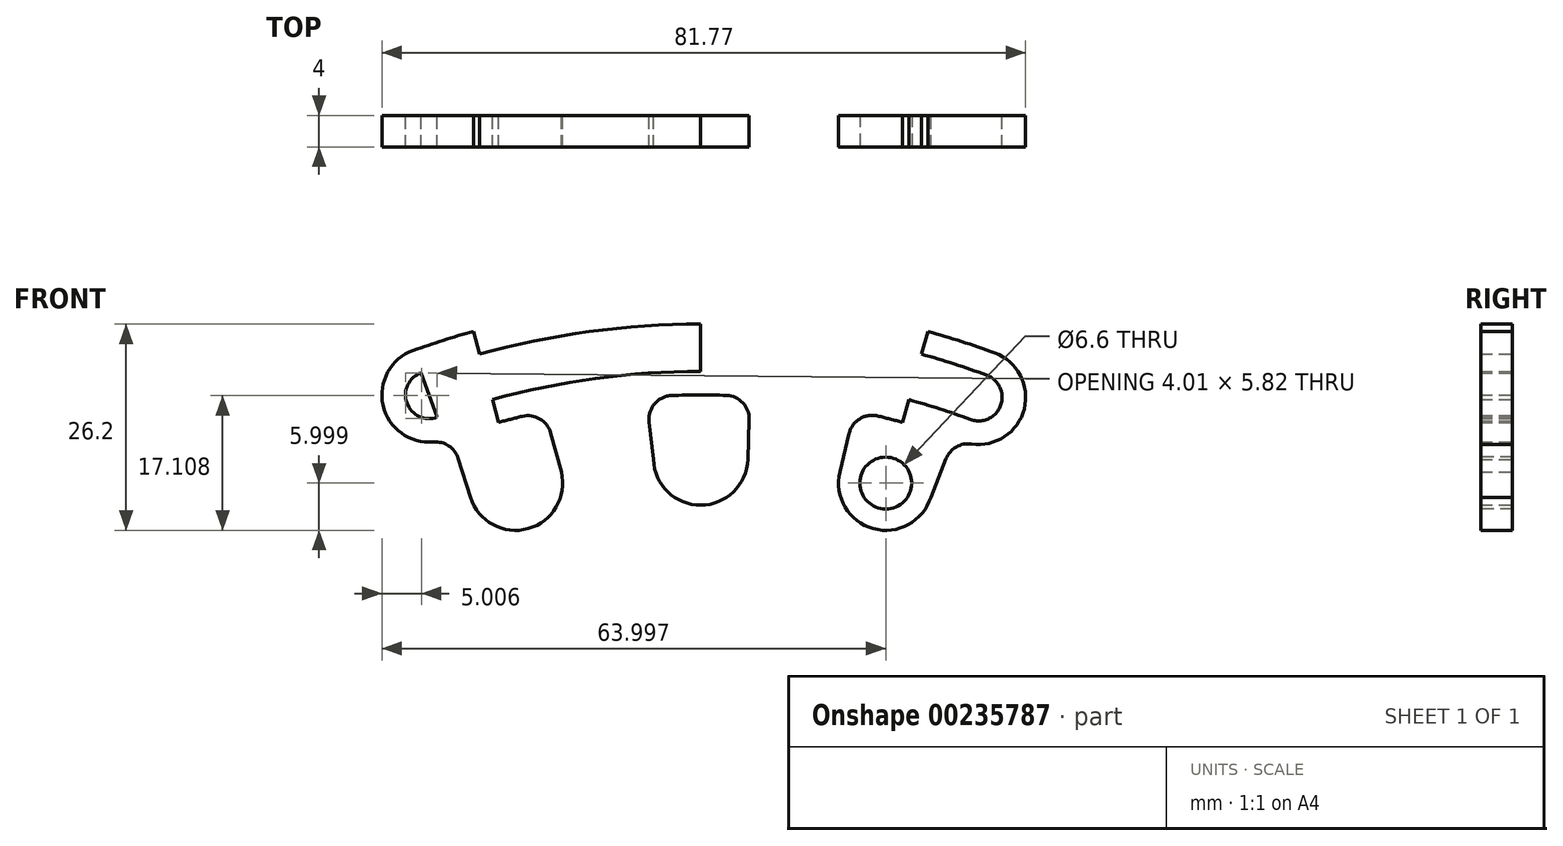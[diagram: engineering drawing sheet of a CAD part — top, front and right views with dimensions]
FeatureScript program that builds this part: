
annotation { "Feature Type Name" : "Feature", "Feature Type Description" : "" }
export const myFeature = defineFeature(function(context is Context, id is Id, definition is map)
    precondition{}
    {
        {
            var Q0;
            Q0=qCreatedBy(makeId("Front.planeOp"),FACE);
            var sketch = newSketch(context, id + "F0", { "sketchPlane" : qUnion([Q0])});
            skArc(sketch, "E0", {"start": v(-36.51, 101.64) * mm, "mid": v(0.45, 108) * mm, "end": v(37.36, 101.33) * mm});
            skLineSegment(sketch, "E1", {"start": v(-36.51, 101.64) * mm, "end": v(0, 0) * mm});
            skLineSegment(sketch, "E2", {"start": v(37.36, 101.33) * mm, "end": v(0, 0) * mm});
            skArc(sketch, "E3", {"start": v(-35.5, 98.82) * mm, "mid": v(0.44, 105) * mm, "end": v(36.33, 98.52) * mm});
            skArc(sketch, "E4", {"start": v(-33.47, 93.17) * mm, "mid": v(0.42, 99) * mm, "end": v(34.25, 92.89) * mm});
            skArc(sketch, "E5", {"start": v(-35.5, 98.82) * mm, "mid": v(-37.3, 94.98) * mm, "end": v(-33.47, 93.17) * mm});
            skArc(sketch, "E6", {"start": v(34.25, 92.89) * mm, "mid": v(38.1, 94.66) * mm, "end": v(36.33, 98.52) * mm});
            skLineSegment(sketch, "E7", {"start": v(0, 0) * mm, "end": v(28.86, 104.07) * mm});
            skLineSegment(sketch, "E8", {"start": v(0, 0) * mm, "end": v(-28.86, 104.07) * mm});
            skLineSegment(sketch, "E9", {"start": v(0, 0) * mm, "end": v(0, 108) * mm});
            skArc(sketch, "E10", {"start": v(-29.75, 82.82) * mm, "mid": v(0.37, 88) * mm, "end": v(30.44, 82.57) * mm});
            skArc(sketch, "E11", {"start": v(-6, 87.8) * mm, "mid": v(0, 82) * mm, "end": v(6, 87.8) * mm});
            skArc(sketch, "E12", {"start": v(-36.51, 101.64) * mm, "mid": v(-40.13, 93.97) * mm, "end": v(-32.45, 90.35) * mm});
            skArc(sketch, "E13", {"start": v(37.36, 101.33) * mm, "mid": v(40.92, 93.63) * mm, "end": v(33.21, 90.07) * mm});
            skArc(sketch, "E14.0", {"start": v(-32.45, 90.35) * mm, "mid": v(0.4, 96) * mm, "end": v(33.21, 90.07) * mm});
            skArc(sketch, "E15", {"start": v(-29.24, 83) * mm, "mid": v(-21.91, 79.02) * mm, "end": v(-17.68, 86.2) * mm});
            skArc(sketch, "E16", {"start": v(17.68, 86.2) * mm, "mid": v(21.91, 79.02) * mm, "end": v(29.24, 83) * mm});
            skLineSegment(sketch, "E17", {"start": v(17.68, 86.2) * mm, "end": v(19.56, 93.99) * mm});
            skLineSegment(sketch, "E18", {"start": v(29.24, 83) * mm, "end": v(32.2, 90.44) * mm});
            skLineSegment(sketch, "E19", {"start": v(-6, 87.8) * mm, "end": v(-6.9, 95.75) * mm});
            skLineSegment(sketch, "E20", {"start": v(-17.68, 86.2) * mm, "end": v(-19.83, 93.93) * mm});
            skLineSegment(sketch, "E21", {"start": v(-29.24, 83) * mm, "end": v(-31.64, 90.64) * mm});
            skLineSegment(sketch, "E22", {"start": v(6, 87.8) * mm, "end": v(6.27, 95.8) * mm});
            skSolve(sketch);
        }
        {
            var Q0;
            {var subQ4=sQuery(id+"F0.wireOp",EDGE,"E4");var subQ6=sQuery(id+"F0.wireOp",EDGE,"E8");var subQ7=makeQuery(id+"F0.imprint","INTERSECT",VERTEX,{"derivedFrom":[subQ4,subQ6]});Q0=makeQuery(id+"F0.imprint","IMPRINT",FACE,{"disambiguationData":[TD([[makeQuery(id+"F0.imprint","IMPRINT",EDGE,{"disambiguationData":[TD([[subQ7,1.0]])],"derivedFrom":subQ6}),1.0]])]});}
            var Q1;
            {var subQ2=sQuery(id+"F0.wireOp",EDGE,"E8");var subQ5=sQuery(id+"F0.wireOp",EDGE,"E4");var subQ8=makeQuery(id+"F0.imprint","INTERSECT",VERTEX,{"derivedFrom":[subQ5,subQ2]});Q1=makeQuery(id+"F0.imprint","IMPRINT",FACE,{"disambiguationData":[TD([[makeQuery(id+"F0.imprint","IMPRINT",EDGE,{"disambiguationData":[TD([[subQ8,-1.0]])],"derivedFrom":subQ5}),-1.0]])]});}
            var Q2;
            {var subQ5=sQuery(id+"F0.wireOp",EDGE,"E20");Q2=makeQuery(id+"F0.imprint","IMPRINT",FACE,{"disambiguationData":[TD([[makeQuery(id+"F0.imprint","IMPRINT",EDGE,{"derivedFrom":subQ5}),1.0]])]});}
            var Q3;
            {var subQ5=sQuery(id+"F0.wireOp",EDGE,"E21");Q3=makeQuery(id+"F0.imprint","IMPRINT",FACE,{"disambiguationData":[TD([[makeQuery(id+"F0.imprint","IMPRINT",EDGE,{"derivedFrom":subQ5}),-1.0]])]});}
            var Q4;
            {var subQ0=sQuery(id+"F0.wireOp",EDGE,"E15");var subQ1=sQuery(id+"F0.wireOp",EDGE,"E8");var subQ2=makeQuery(id+"F0.imprint","INTERSECT",VERTEX,{"derivedFrom":[subQ1,subQ0]});Q4=makeQuery(id+"F0.imprint","IMPRINT",FACE,{"disambiguationData":[TD([[makeQuery(id+"F0.imprint","IMPRINT",EDGE,{"disambiguationData":[TD([[subQ2,-1.0]])],"derivedFrom":subQ1}),1.0]])]});}
            var Q5;
            {var subQ0=sQuery(id+"F0.wireOp",EDGE,"E15");var subQ1=sQuery(id+"F0.wireOp",EDGE,"E8");var subQ2=makeQuery(id+"F0.imprint","INTERSECT",VERTEX,{"derivedFrom":[subQ1,subQ0]});Q5=makeQuery(id+"F0.imprint","IMPRINT",FACE,{"disambiguationData":[TD([[makeQuery(id+"F0.imprint","IMPRINT",EDGE,{"disambiguationData":[TD([[subQ2,-1.0]])],"derivedFrom":subQ1}),-1.0]])]});}
            var Q6;
            {var subQ5=sQuery(id+"F0.wireOp",EDGE,"E19");Q6=makeQuery(id+"F0.imprint","IMPRINT",FACE,{"disambiguationData":[TD([[makeQuery(id+"F0.imprint","IMPRINT",EDGE,{"derivedFrom":subQ5}),-1.0]])]});}
            var Q7;
            {var subQ5=sQuery(id+"F0.wireOp",EDGE,"E22");Q7=makeQuery(id+"F0.imprint","IMPRINT",FACE,{"disambiguationData":[TD([[makeQuery(id+"F0.imprint","IMPRINT",EDGE,{"derivedFrom":subQ5}),1.0]])]});}
            var Q8;
            {var subQ0=sQuery(id+"F0.wireOp",EDGE,"E11");var subQ1=sQuery(id+"F0.wireOp",EDGE,"E9");var subQ2=makeQuery(id+"F0.imprint","INTERSECT",VERTEX,{"derivedFrom":[subQ1,subQ0]});Q8=makeQuery(id+"F0.imprint","IMPRINT",FACE,{"disambiguationData":[TD([[makeQuery(id+"F0.imprint","IMPRINT",EDGE,{"disambiguationData":[TD([[subQ2,-1.0]])],"derivedFrom":subQ1}),-1.0]])]});}
            var Q9;
            {var subQ0=sQuery(id+"F0.wireOp",EDGE,"E11");var subQ1=sQuery(id+"F0.wireOp",EDGE,"E9");var subQ2=makeQuery(id+"F0.imprint","INTERSECT",VERTEX,{"derivedFrom":[subQ1,subQ0]});Q9=makeQuery(id+"F0.imprint","IMPRINT",FACE,{"disambiguationData":[TD([[makeQuery(id+"F0.imprint","IMPRINT",EDGE,{"disambiguationData":[TD([[subQ2,-1.0]])],"derivedFrom":subQ1}),1.0]])]});}
            var Q10;
            {var subQ2=sQuery(id+"F0.wireOp",EDGE,"E9");var subQ4=sQuery(id+"F0.wireOp",EDGE,"E4");var subQ5=makeQuery(id+"F0.imprint","INTERSECT",VERTEX,{"derivedFrom":[subQ4,subQ2]});Q10=makeQuery(id+"F0.imprint","IMPRINT",FACE,{"disambiguationData":[TD([[makeQuery(id+"F0.imprint","IMPRINT",EDGE,{"disambiguationData":[TD([[subQ5,-1.0]])],"derivedFrom":subQ4}),-1.0]])]});}
            var Q11;
            {var subQ2=sQuery(id+"F0.wireOp",EDGE,"E5");Q11=makeQuery(id+"F0.imprint","IMPRINT",FACE,{"disambiguationData":[TD([[makeQuery(id+"F0.imprint","IMPRINT",EDGE,{"derivedFrom":subQ2}),-1.0]])]});}
            var Q12;
            {var subQ1=sQuery(id+"F0.wireOp",EDGE,"E0");var subQ3=sQuery(id+"F0.wireOp",EDGE,"E8");var subQ4=makeQuery(id+"F0.imprint","INTERSECT",VERTEX,{"derivedFrom":[subQ1,subQ3]});Q12=makeQuery(id+"F0.imprint","IMPRINT",FACE,{"disambiguationData":[TD([[makeQuery(id+"F0.imprint","IMPRINT",EDGE,{"disambiguationData":[TD([[subQ4,1.0]])],"derivedFrom":subQ3}),1.0]])]});}
            var Q13;
            {var subQ0=sQuery(id+"F0.wireOp",EDGE,"E8");var subQ1=sQuery(id+"F0.wireOp",EDGE,"E0");var subQ2=makeQuery(id+"F0.imprint","INTERSECT",VERTEX,{"derivedFrom":[subQ1,subQ0]});Q13=makeQuery(id+"F0.imprint","IMPRINT",FACE,{"disambiguationData":[TD([[makeQuery(id+"F0.imprint","IMPRINT",EDGE,{"disambiguationData":[TD([[subQ2,-1.0]])],"derivedFrom":subQ1}),-1.0]])]});}
            var Q14;
            {var subQ0=sQuery(id+"F0.wireOp",EDGE,"E7");var subQ1=sQuery(id+"F0.wireOp",EDGE,"E0");var subQ2=makeQuery(id+"F0.imprint","INTERSECT",VERTEX,{"derivedFrom":[subQ1,subQ0]});Q14=makeQuery(id+"F0.imprint","IMPRINT",FACE,{"disambiguationData":[TD([[makeQuery(id+"F0.imprint","IMPRINT",EDGE,{"disambiguationData":[TD([[subQ2,1.0]])],"derivedFrom":subQ1}),-1.0]])]});}
            var Q15;
            {var subQ1=sQuery(id+"F0.wireOp",EDGE,"E0");var subQ3=sQuery(id+"F0.wireOp",EDGE,"E7");var subQ4=makeQuery(id+"F0.imprint","INTERSECT",VERTEX,{"derivedFrom":[subQ1,subQ3]});Q15=makeQuery(id+"F0.imprint","IMPRINT",FACE,{"disambiguationData":[TD([[makeQuery(id+"F0.imprint","IMPRINT",EDGE,{"disambiguationData":[TD([[subQ4,1.0]])],"derivedFrom":subQ3}),-1.0]])]});}
            var Q16;
            {var subQ2=sQuery(id+"F0.wireOp",EDGE,"E6");Q16=makeQuery(id+"F0.imprint","IMPRINT",FACE,{"disambiguationData":[TD([[makeQuery(id+"F0.imprint","IMPRINT",EDGE,{"derivedFrom":subQ2}),-1.0]])]});}
            var Q17;
            {var subQ0=sQuery(id+"F0.wireOp",EDGE,"E7");var subQ1=sQuery(id+"F0.wireOp",EDGE,"E4");var subQ2=makeQuery(id+"F0.imprint","INTERSECT",VERTEX,{"derivedFrom":[subQ1,subQ0]});Q17=makeQuery(id+"F0.imprint","IMPRINT",FACE,{"disambiguationData":[TD([[makeQuery(id+"F0.imprint","IMPRINT",EDGE,{"disambiguationData":[TD([[subQ2,1.0]])],"derivedFrom":subQ0}),-1.0]])]});}
            var Q18;
            {var subQ5=sQuery(id+"F0.wireOp",EDGE,"E18");Q18=makeQuery(id+"F0.imprint","IMPRINT",FACE,{"disambiguationData":[TD([[makeQuery(id+"F0.imprint","IMPRINT",EDGE,{"derivedFrom":subQ5}),1.0]])]});}
            var Q19;
            {var subQ5=sQuery(id+"F0.wireOp",EDGE,"E17");Q19=makeQuery(id+"F0.imprint","IMPRINT",FACE,{"disambiguationData":[TD([[makeQuery(id+"F0.imprint","IMPRINT",EDGE,{"derivedFrom":subQ5}),-1.0]])]});}
            var Q20;
            {var subQ0=sQuery(id+"F0.wireOp",EDGE,"E16");var subQ1=sQuery(id+"F0.wireOp",EDGE,"E7");var subQ2=makeQuery(id+"F0.imprint","INTERSECT",VERTEX,{"derivedFrom":[subQ1,subQ0]});Q20=makeQuery(id+"F0.imprint","IMPRINT",FACE,{"disambiguationData":[TD([[makeQuery(id+"F0.imprint","IMPRINT",EDGE,{"disambiguationData":[TD([[subQ2,-1.0]])],"derivedFrom":subQ1}),1.0]])]});}
            var Q21;
            {var subQ0=sQuery(id+"F0.wireOp",EDGE,"E16");var subQ1=sQuery(id+"F0.wireOp",EDGE,"E7");var subQ2=makeQuery(id+"F0.imprint","INTERSECT",VERTEX,{"derivedFrom":[subQ1,subQ0]});Q21=makeQuery(id+"F0.imprint","IMPRINT",FACE,{"disambiguationData":[TD([[makeQuery(id+"F0.imprint","IMPRINT",EDGE,{"disambiguationData":[TD([[subQ2,-1.0]])],"derivedFrom":subQ1}),-1.0]])]});}
            extrude(context, id + "F1", {"entities" : qUnion([Q0, Q1, Q2, Q3, Q4, Q5, Q6, Q7, Q8, Q9, Q10, Q11, Q12, Q13, Q14, Q15, Q16, Q17, Q18, Q19, Q20, Q21]), "depth" : 4 * mm});
        }
        {
            var Q0;
            Q0=makeQuery(id+"F1.opExtrude","CAP_FACE",FACE,{"disambiguationData":[OSD([sQuery(id+"F0.wireOp",EDGE,"E0"),sQuery(id+"F0.wireOp",EDGE,"E3"),sQuery(id+"F0.wireOp",EDGE,"E4"),sQuery(id+"F0.wireOp",EDGE,"E5"),sQuery(id+"F0.wireOp",EDGE,"E6"),sQuery(id+"F0.wireOp",EDGE,"E11"),sQuery(id+"F0.wireOp",EDGE,"E12"),sQuery(id+"F0.wireOp",EDGE,"E13"),sQuery(id+"F0.wireOp",EDGE,"E14.0"),sQuery(id+"F0.wireOp",EDGE,"E15"),sQuery(id+"F0.wireOp",EDGE,"E16"),sQuery(id+"F0.wireOp",EDGE,"E17"),sQuery(id+"F0.wireOp",EDGE,"E18"),sQuery(id+"F0.wireOp",EDGE,"E19"),sQuery(id+"F0.wireOp",EDGE,"E20"),sQuery(id+"F0.wireOp",EDGE,"E21"),sQuery(id+"F0.wireOp",EDGE,"E22")])],"isStart":false});
            var sketch = newSketch(context, id + "F2", { "sketchPlane" : qUnion([Q0])});
            skCircle(sketch, "E23", {"center": v(-23.52, 84.8) * mm, "radius": 3.3 * mm});
            skCircle(sketch, "E24.MirrorC", {"center": v(23.52, 84.8) * mm, "radius": 3.3 * mm});
            skCircle(sketch, "E25", {"center": v(0, 87.8) * mm, "radius": 3.3 * mm});
            skSolve(sketch);
        }
        {
            var Q0;
            Q0=sQuery(id+"F2.wireOp",VERTEX,"E23.center");
            var Q1;
            Q1=sQuery(id+"F2.wireOp",VERTEX,"E25.center");
            var Q2;
            Q2=sQuery(id+"F2.wireOp",VERTEX,"E24.MirrorC.center");
            var Q3;
            Q3=makeQuery(id+"F1.opExtrude","SWEPT_BODY",BODY,{"disambiguationData":[OSD([sQuery(id+"F0.wireOp",EDGE,"E0"),sQuery(id+"F0.wireOp",EDGE,"E3"),sQuery(id+"F0.wireOp",EDGE,"E4"),sQuery(id+"F0.wireOp",EDGE,"E5"),sQuery(id+"F0.wireOp",EDGE,"E6"),sQuery(id+"F0.wireOp",EDGE,"E11"),sQuery(id+"F0.wireOp",EDGE,"E12"),sQuery(id+"F0.wireOp",EDGE,"E13"),sQuery(id+"F0.wireOp",EDGE,"E14.0"),sQuery(id+"F0.wireOp",EDGE,"E15"),sQuery(id+"F0.wireOp",EDGE,"E16"),sQuery(id+"F0.wireOp",EDGE,"E17"),sQuery(id+"F0.wireOp",EDGE,"E18"),sQuery(id+"F0.wireOp",EDGE,"E19"),sQuery(id+"F0.wireOp",EDGE,"E20"),sQuery(id+"F0.wireOp",EDGE,"E21"),sQuery(id+"F0.wireOp",EDGE,"E22")])]});
            hole(context, id + "F3", {"style" : HoleStyle.SIMPLE, "endStyle" : HoleEndStyle.THROUGH, "holeDiameter" : 6.6 * mm, "locations" : qUnion([Q0, Q1, Q2]), "scope" : qUnion([Q3]), "isTappedThrough" : true});
        }
        {
            var Q0;
            Q0=makeQuery(id+"F1.opExtrude","SWEPT_EDGE",EDGE,{"disambiguationData":[OSD([sQuery(id+"F0.wireOp",EDGE,"E14.0"),sQuery(id+"F0.wireOp",EDGE,"E20")])]});
            var Q1;
            Q1=makeQuery(id+"F1.opExtrude","SWEPT_EDGE",EDGE,{"disambiguationData":[OSD([sQuery(id+"F0.wireOp",EDGE,"E14.0"),sQuery(id+"F0.wireOp",EDGE,"E22")])]});
            var Q2;
            Q2=makeQuery(id+"F1.opExtrude","SWEPT_EDGE",EDGE,{"disambiguationData":[OSD([sQuery(id+"F0.wireOp",EDGE,"E14.0"),sQuery(id+"F0.wireOp",EDGE,"E21")])]});
            var Q3;
            Q3=makeQuery(id+"F1.opExtrude","SWEPT_EDGE",EDGE,{"disambiguationData":[OSD([sQuery(id+"F0.wireOp",EDGE,"E14.0"),sQuery(id+"F0.wireOp",EDGE,"E19")])]});
            var Q4;
            Q4=makeQuery(id+"F1.opExtrude","SWEPT_EDGE",EDGE,{"disambiguationData":[OSD([sQuery(id+"F0.wireOp",EDGE,"E14.0"),sQuery(id+"F0.wireOp",EDGE,"E17")])]});
            var Q5;
            Q5=makeQuery(id+"F1.opExtrude","SWEPT_EDGE",EDGE,{"disambiguationData":[OSD([sQuery(id+"F0.wireOp",EDGE,"E14.0"),sQuery(id+"F0.wireOp",EDGE,"E18")])]});
            fillet(context, id + "F4", {"entities" : qUnion([Q0, Q1, Q2, Q3, Q4, Q5]), "radius" : 3 * mm, "tangentPropagation" : true, "allowEdgeOverflow" : false});
        }
    });
